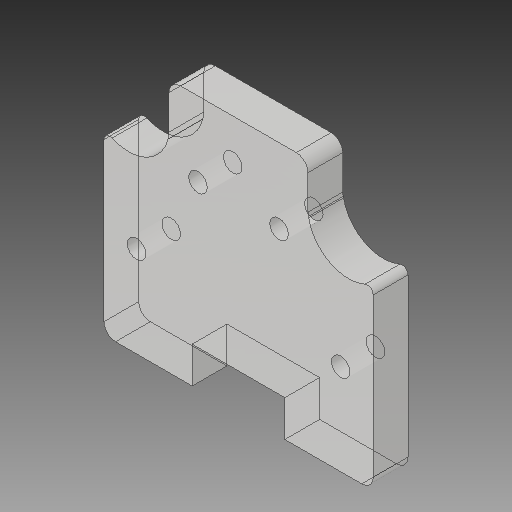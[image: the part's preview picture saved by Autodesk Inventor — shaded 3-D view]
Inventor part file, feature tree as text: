
AUTODESK INVENTOR PART (.ipt)
format: ipt  version: 2018 (Build 220112000, 112)  size: 164,864 bytes
history: native  units: mm
features: sketch x4, other x3, plane x1
ambient origin geometry x8: Origin, YZ Plane, XZ Plane, XY Plane, X Axis, Y Axis, Z Axis, Center Point
bodies: Solid1 (feature_tree)
feature tree (8):
  other  "Hotend Slide Part3.ipt"
  other  "Solid1::Hotend Slide Part3.ipt"
  other  "TaggingFeature1"
  sketch  "Sketch1"  dims[d0=10.0mm]
  sketch  "Sketch2"
  sketch  "Sketch3"
  sketch  "Sketch4"
  plane  "Work Plane1"
